# Revit family: Fireplace_Gas_Heatilator_Reveal
name_source: partatom
category: Mechanical Equipment
revit_build: Autodesk Revit 2015 (Build: 20140323_1530(x64)
units: mm (PartAtom-declared; Revit-internal decimal feet)

## types (4) — shared parameters
Assembly Code = D3020
Construction Details = http://www.arcat.com
Default Elevation = 0' - 0"
Efficiency Ratings = as Specified
Electrical_Voltage = 120 V
Fixture Finish = Metal - Heatilator - Metallic Black
Fuel Consumption = as Specified
HVAC_BTU Output = 0.0 Btu/h
Heating Capacity = as Specified
Keynote = 10305
Manufacturer = Heatilator
Manufacturer Website = http://www.heatilator.com
Opening Height = 1' - 9"
Product Data = http://www.arcat.com
Revision = R2_2014-09
Sales Information = http://www.heatilator.com
Send Message = http://www.arcat.com
Specification = http://www.arcat.com
Standards Conformance = UL  ;  cUL
URL = http://www.heatilator.com
Unit Depth = 1' - 9 1/2"
Unit Height = 3' - 3 1/2"
zero-valued in all types: Expected Lifespan (Years), Maintenance Schedule (Months), Unit Weight, Warranty Duration (Years)

## per-type parameters (varying)
| type | Description | Fuel Type | HVAC_BTU Input | Model | Opening Width | Rear Width | Unit Width |
| 42x21 Viewing Area LP | Heatilator Gas Burning Fireplace - Reveal RBV4842 LP as Specified | LP | 41000.0 Btu/h | RBV4842 | 3' - 6" | 2' - 5 3/4" | 3' - 11" |
| 42x21 Viewing Area NG | Heatilator Gas Burning Fireplace - Reveal RBV4842 NG as Specified | NG | 43000.0 Btu/h | RBV4842 | 3' - 6" | 2' - 5 3/4" | 3' - 11" |
| 36x21 Viewing Area LP | Heatilator Gas Burning Fireplace - Reveal RBV4236 LP as Specified | LP | 38000.0 Btu/h | RBV4236 | 3' - 0" | 1' - 11 3/4" | 3' - 5" |
| 36x21 Viewing Area NG | Heatilator Gas Burning Fireplace - Reveal RBV4236 NG as Specified | NG | 40000.0 Btu/h | RBV4236 | 3' - 0" | 1' - 11 3/4" | 3' - 5" |

## geometry (parser evidence)
native form markers: Blend x10, Sweep x5
no freeform markers — native parametric forms only
